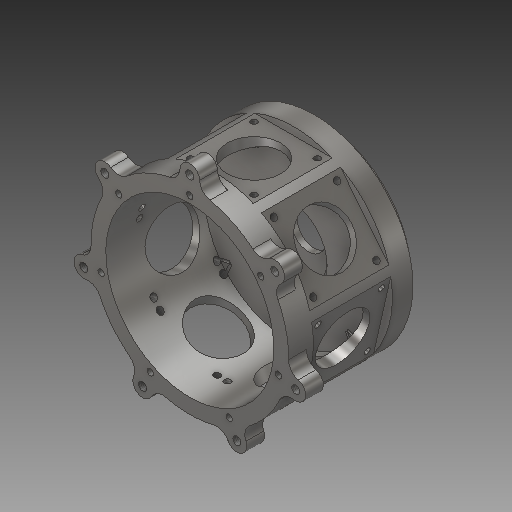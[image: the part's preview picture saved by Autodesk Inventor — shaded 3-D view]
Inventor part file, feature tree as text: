
AUTODESK INVENTOR PART (.ipt)
format: ipt  version: 2018 (Build 220112000, 112)  size: 628,736 bytes
history: native  units: mm
features: sketch x10, extrude x10, hole x4, pattern_circular x2, direct_edit x1, chamfer x1, other x1, revolve x1, projected_geometry x1
ambient origin geometry x8: Origin, YZ Plane, XZ Plane, XY Plane, X Axis, Y Axis, Z Axis, Center Point
bodies: Solid1 (feature_tree)
feature tree (31):
  sketch  "Sketch1"  dims[d0=100.0mm d1=90.0mm]
  extrude  "Extrusion1"  Depth=90.0mm
  extrude  "Extrusion2"  Depth=67.0mm TaperAngle=0.0deg
  extrude  "Extrusion3"  Depth=4.07mm
  extrude  "Extrusion4"  Depth=13.0mm TaperAngle=0.0deg
  extrude  "Extrusion5"  Depth=18.0mm
  direct_edit  "Direct Edit1"
  extrude  "Extrusion6"  Depth=12.0mm
  extrude  "Extrusion7"  Depth=30.0mm TaperAngle=360.0deg
  chamfer  "Chamfer1"  Distance=9.0mm
  extrude  "Extrusion8"  Depth=5.0mm
  sketch  "Sketch8"  dims[d28=8.0mm d29=30.0mm d31=360.0deg]
  extrude  "Extrusion9"  Depth=10.0mm TaperAngle=0.0deg
  hole  "Hole1"  [1 undecoded]
  extrude  "Extrusion10"  Depth=5.0mm TaperAngle=0.0deg
  hole  "Hole2"  [1 undecoded]
  hole  "Hole3"  [1 undecoded]
  other  "Work Axis1"
  pattern_circular  "Circular Pattern1"  [2 undecoded]
  hole  "Hole4"  [1 undecoded]
  pattern_circular  "Circular Pattern2"  [2 undecoded]
  sketch  "Sketch2"  dims[d2=80.0mm d3=67.0mm d4=0.0mm]
  sketch  "Sketch4"  dims[d5=4.07mm d6=0.0mm d7=85.0mm]
  sketch  "Sketch5"  dims[d8=50.0mm d9=0.0mm d10=13.0mm d11=0.0mm]
  sketch  "Sketch6"  dims[d12=43.0mm d22=21.5mm d25=18.0mm]
  sketch  "Sketch7"  dims[d26=25.0mm d27=12.0mm]
  sketch  "Sketch9"  dims[d33=21.5mm]
  sketch  "Sketch10"  dims[d34=21.5mm d35=9.0mm d36=0.0mm]
  sketch  "Sketch11"  dims[d37=-15.707963mm d38=35.0mm d39=10.0mm d40=0.0mm d41=17.35mm d42=17.0mm d43=0.0mm d44=2.0mm d45=2.0mm d46=45.0deg d47=40.0mm d48=10.43mm d49=46.0mm d50=39.19mm d51=0.0mm d53=39.19mm d54=0.0mm d55=27.0mm d57=19.595mm d58=32.0mm d59=32.0mm d60=3.242mm d61=8.0mm d62=3.023mm d63=2.0mm d64=14.3117mm d65=11.8mm d66=20.594885mm d67=20.0mm d69=13.0mm d70=9.0mm d71=0.0mm d72=10.0mm d73=10.0mm d74=4.134mm d75=10.0mm d76=3.023mm d77=2.0mm d78=14.3117mm d79=14.2mm d80=20.594885mm d81=46.0mm d82=3.242mm d83=8.0mm d84=3.023mm d85=2.0mm d86=14.3117mm d87=10.8mm d88=20.594885mm d89=70.0mm d90=360.0deg d92=85.0mm d93=3.242mm d94=8.0mm d95=3.023mm d96=2.0mm d97=14.3117mm d98=13.3mm d99=20.594885mm d100=70.0mm d101=360.0deg d103=55.0mm d104=5.0mm]
  revolve  "Rotate1"  [1 undecoded]
  projected_geometry  "Project Cut Edges1"
note: 9 required parameter values undecoded (feature->parameter linkage not recoverable at this tier; creation-order binding heuristic only, values carry confidence <= 0.55)